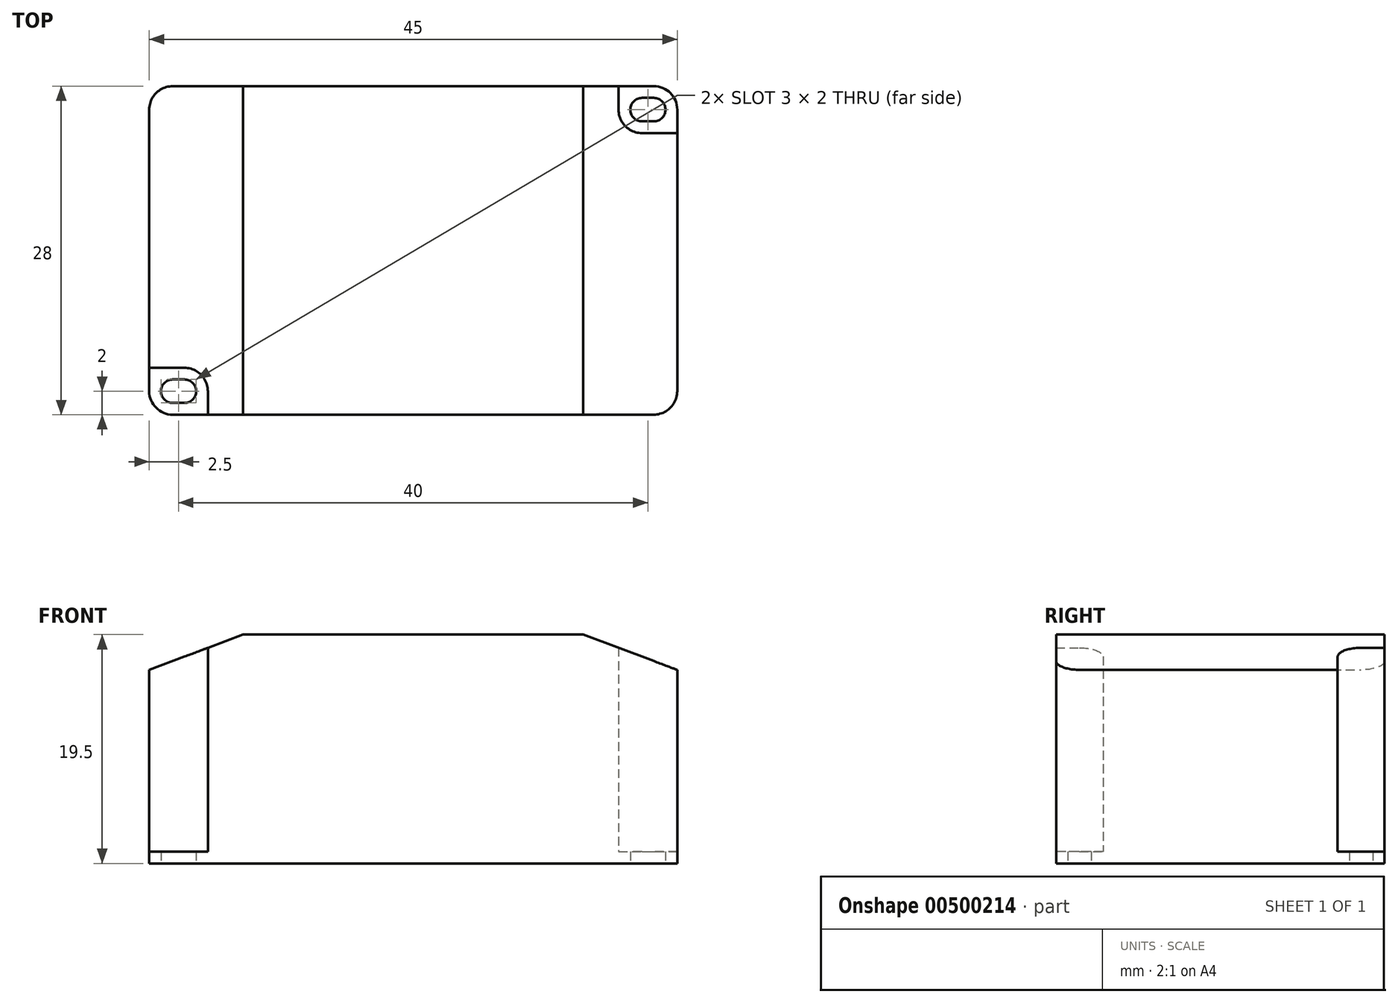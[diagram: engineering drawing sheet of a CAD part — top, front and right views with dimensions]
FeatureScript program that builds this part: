
annotation { "Feature Type Name" : "Feature", "Feature Type Description" : "" }
export const myFeature = defineFeature(function(context is Context, id is Id, definition is map)
    precondition{}
    {
        {
            var Q0;
            Q0=qCreatedBy(makeId("Top.planeOp"),FACE);
            var sketch = newSketch(context, id + "F0", { "sketchPlane" : qUnion([Q0])});
            skLineSegment(sketch, "E0.bottom", {"start": v(-22.5, 14) * mm, "end": v(22.5, 14) * mm});
            skLineSegment(sketch, "E0.top", {"start": v(-22.5, -14) * mm, "end": v(22.5, -14) * mm});
            skLineSegment(sketch, "E0.left", {"start": v(-22.5, 14) * mm, "end": v(-22.5, -14) * mm});
            skLineSegment(sketch, "E0.right", {"start": v(22.5, 14) * mm, "end": v(22.5, -14) * mm});
            skLineSegment(sketch, "E1", {"start": v(-22.5, -10) * mm, "end": v(-17.5, -10) * mm});
            skLineSegment(sketch, "E2", {"start": v(-17.5, -10) * mm, "end": v(-17.5, -14) * mm});
            skLineSegment(sketch, "E3", {"start": v(17.5, 14) * mm, "end": v(17.5, 10) * mm});
            skLineSegment(sketch, "E4", {"start": v(17.5, 10) * mm, "end": v(22.5, 10) * mm});
            skArc(sketch, "E5", {"start": v(-20.5, -11) * mm, "mid": v(-21.5, -12) * mm, "end": v(-20.5, -13) * mm});
            skArc(sketch, "E6", {"start": v(-19.5, -13) * mm, "mid": v(-18.5, -12) * mm, "end": v(-19.5, -11) * mm});
            skLineSegment(sketch, "E7", {"start": v(-20.5, -11) * mm, "end": v(-19.5, -11) * mm});
            skLineSegment(sketch, "E8", {"start": v(-20.5, -13) * mm, "end": v(-19.5, -13) * mm});
            skPoint(sketch, "E9", {"position": v(-20, -12) * mm});
            skArc(sketch, "E10", {"start": v(19.5, 13) * mm, "mid": v(18.5, 12) * mm, "end": v(19.5, 11) * mm});
            skArc(sketch, "E11", {"start": v(20.5, 11) * mm, "mid": v(21.5, 12) * mm, "end": v(20.5, 13) * mm});
            skLineSegment(sketch, "E12", {"start": v(19.5, 13) * mm, "end": v(20.5, 13) * mm});
            skLineSegment(sketch, "E13", {"start": v(19.5, 11) * mm, "end": v(20.5, 11) * mm});
            skPoint(sketch, "E14", {"position": v(20, 12) * mm});
            skSolve(sketch);
        }
        {
            var Q0;
            Q0 = qSketchRegion(id + "F0", true);
            extrude(context, id + "F1", {"entities" : qUnion([Q0]), "depth" : 19.5 * mm, "offsetDistance" : 25 * mm});
        }
        {
            var Q0;
            Q0=makeQuery(id+"F1.opExtrude","CAP_EDGE",EDGE,{"disambiguationData":[OSD([sQuery(id+"F0.wireOp",EDGE,"E0.left")])],"isStart":false});
            var Q1;
            Q1=makeQuery(id+"F1.opExtrude","CAP_EDGE",EDGE,{"disambiguationData":[OSD([sQuery(id+"F0.wireOp",EDGE,"E0.right")])],"isStart":false});
            chamfer(context, id + "F2", {"entities" : qUnion([Q0, Q1]), "chamferType" : ChamferType.TWO_OFFSETS, "width1" : 3 * mm, "oppositeDirection" : true, "width2" : 8 * mm, "tangentPropagation" : true});
        }
        {
            var Q0;
            {var subQ1=sQuery(id+"F0.wireOp",EDGE,"E1");Q0=makeQuery(id+"F0.imprint","IMPRINT",FACE,{"disambiguationData":[TD([[makeQuery(id+"F0.imprint","IMPRINT",EDGE,{"derivedFrom":subQ1}),-1.0]])]});}
            var Q1;
            {var subQ0=sQuery(id+"F0.wireOp",EDGE,"E3");Q1=makeQuery(id+"F0.imprint","IMPRINT",FACE,{"disambiguationData":[TD([[makeQuery(id+"F0.imprint","IMPRINT",EDGE,{"derivedFrom":subQ0}),1.0]])]});}
            extrude(context, id + "F3", {"entities" : qUnion([Q0, Q1]), "operationType" : NewBodyOperationType.REMOVE, "depth" : 25 * mm, "offsetDistance" : 25 * mm, "hasSecondDirection" : true, "secondDirectionOppositeDirection" : false, "secondDirectionDepth" : 1 * mm});
        }
        {
            var Q0;
            Q0=makeQuery(id+"F3.boolean.opBoolean","COPY",EDGE,{"derivedFrom":makeQuery(id+"F3.opExtrude","SWEPT_EDGE",EDGE,{"disambiguationData":[OSD([sQuery(id+"F0.wireOp",EDGE,"E1"),sQuery(id+"F0.wireOp",EDGE,"E2")])]})});
            var Q1;
            Q1=makeQuery(id+"F3.boolean.opBoolean","COPY",EDGE,{"derivedFrom":makeQuery(id+"F3.opExtrude","SWEPT_EDGE",EDGE,{"disambiguationData":[OSD([sQuery(id+"F0.wireOp",EDGE,"E3"),sQuery(id+"F0.wireOp",EDGE,"E4")])]})});
            var Q2;
            Q2=makeQuery(id+"F1.opExtrude","SWEPT_EDGE",EDGE,{"disambiguationData":[OSD([sQuery(id+"F0.wireOp",EDGE,"E0.top"),sQuery(id+"F0.wireOp",EDGE,"E0.right")])]});
            var Q3;
            Q3=makeQuery(id+"F1.opExtrude","SWEPT_EDGE",EDGE,{"disambiguationData":[OSD([sQuery(id+"F0.wireOp",EDGE,"E0.bottom"),sQuery(id+"F0.wireOp",EDGE,"E0.right")])]});
            var Q4;
            Q4=makeQuery(id+"F1.opExtrude","SWEPT_EDGE",EDGE,{"disambiguationData":[OSD([sQuery(id+"F0.wireOp",EDGE,"E0.bottom"),sQuery(id+"F0.wireOp",EDGE,"E0.left")])]});
            var Q5;
            Q5=makeQuery(id+"F1.opExtrude","SWEPT_EDGE",EDGE,{"disambiguationData":[OSD([sQuery(id+"F0.wireOp",EDGE,"E0.top"),sQuery(id+"F0.wireOp",EDGE,"E0.left")])]});
            fillet(context, id + "F4", {"entities" : qUnion([Q0, Q1, Q2, Q3, Q4, Q5]), "radius" : 2 * mm, "tangentPropagation" : true, "allowEdgeOverflow" : false});
        }
    });
